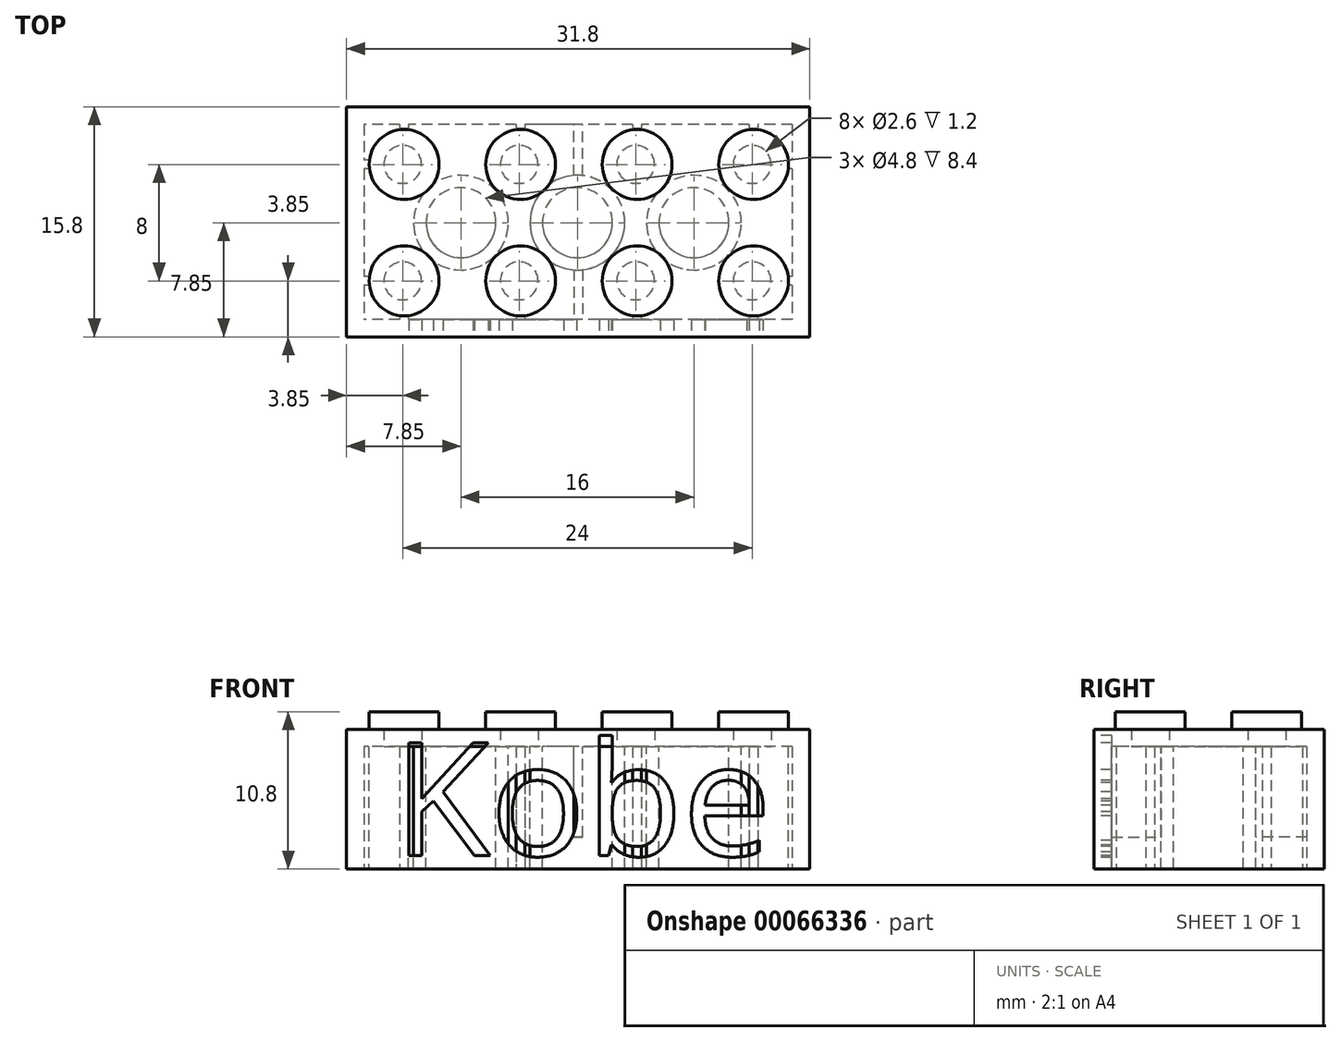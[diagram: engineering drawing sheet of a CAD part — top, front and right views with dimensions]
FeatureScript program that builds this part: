
annotation { "Feature Type Name" : "Feature", "Feature Type Description" : "" }
export const myFeature = defineFeature(function(context is Context, id is Id, definition is map)
    precondition{}
    {
        {
            var Q0;
            Q0=qCreatedBy(makeId("Top.planeOp"),FACE);
            var sketch = newSketch(context, id + "F0", { "sketchPlane" : qUnion([Q0])});
            skLineSegment(sketch, "E0.rect.bottom", {"start": v(15.9, -7.9) * mm, "end": v(-15.9, -7.9) * mm});
            skLineSegment(sketch, "E0.rect.top", {"start": v(15.9, 7.9) * mm, "end": v(-15.9, 7.9) * mm});
            skLineSegment(sketch, "E0.rect.left", {"start": v(15.9, -7.9) * mm, "end": v(15.9, 7.9) * mm});
            skLineSegment(sketch, "E0.rect.right", {"start": v(-15.9, -7.9) * mm, "end": v(-15.9, 7.9) * mm});
            skPoint(sketch, "E0.rect.middle", {"position": v(0, 0) * mm});
            skSolve(sketch);
        }
        {
            var Q0;
            Q0 = qSketchRegion(id + "F0", true);
            extrude(context, id + "F1", {"entities" : qUnion([Q0]), "depth" : 9.6 * mm});
        }
        {
            var Q0;
            Q0=makeQuery(id+"F1.opExtrude","CAP_FACE",FACE,{"disambiguationData":[OSD([sQuery(id+"F0.wireOp",EDGE,"E0.rect.bottom"),sQuery(id+"F0.wireOp",EDGE,"E0.rect.top"),sQuery(id+"F0.wireOp",EDGE,"E0.rect.left"),sQuery(id+"F0.wireOp",EDGE,"E0.rect.right")])],"isStart":true});
            var sketch = newSketch(context, id + "F2", { "sketchPlane" : qUnion([Q0])});
            skLineSegment(sketch, "E1.rect.bottom", {"start": v(14.7, -6.7) * mm, "end": v(-14.7, -6.7) * mm});
            skLineSegment(sketch, "E1.rect.top", {"start": v(14.7, 6.7) * mm, "end": v(-14.7, 6.7) * mm});
            skLineSegment(sketch, "E1.rect.left", {"start": v(14.7, -6.7) * mm, "end": v(14.7, 6.7) * mm});
            skLineSegment(sketch, "E1.rect.right", {"start": v(-14.7, -6.7) * mm, "end": v(-14.7, 6.7) * mm});
            skPoint(sketch, "E1.rect.middle", {"position": v(0, 0) * mm});
            skSolve(sketch);
        }
        {
            var Q0;
            Q0 = qSketchRegion(id + "F2", true);
            extrude(context, id + "F3", {"entities" : qUnion([Q0]), "operationType" : NewBodyOperationType.REMOVE, "oppositeDirection" : true, "depth" : 8.4 * mm});
        }
        {
            var Q0;
            Q0=makeQuery(id+"F1.opExtrude","CAP_FACE",FACE,{"disambiguationData":[OSD([sQuery(id+"F0.wireOp",EDGE,"E0.rect.bottom"),sQuery(id+"F0.wireOp",EDGE,"E0.rect.top"),sQuery(id+"F0.wireOp",EDGE,"E0.rect.left"),sQuery(id+"F0.wireOp",EDGE,"E0.rect.right")])],"isStart":false});
            var sketch = newSketch(context, id + "F4", { "sketchPlane" : qUnion([Q0])});
            skLineSegment(sketch, "E2", {"start": v(0, 0) * mm, "end": v(-19.28, 0) * mm, "construction": true});
            skLineSegment(sketch, "E3", {"start": v(-19.28, 0) * mm, "end": v(19.46, 0) * mm, "construction": true});
            skSolve(sketch);
        }
        {
            var Q0;
            Q0=makeQuery(id+"F4.imprint","IMPRINT",FACE,{"disambiguationData":[TD([[makeQuery(id+"F4.imprint","IMPRINT",EDGE,{"derivedFrom":makeQuery(id+"F1.opExtrude","CAP_EDGE",EDGE,{"disambiguationData":[OSD([sQuery(id+"F0.wireOp",EDGE,"E0.rect.bottom")])],"isStart":false})}),-1.0]])]});
            var sketch = newSketch(context, id + "F5", { "sketchPlane" : qUnion([Q0])});
            skCircle(sketch, "E4", {"center": v(-11.95, 3.95) * mm, "radius": 2.4 * mm});
            skCircle(sketch, "E5.0.1.0", {"center": v(-11.95, -4.05) * mm, "radius": 2.4 * mm});
            skCircle(sketch, "E5.1.0.0", {"center": v(-3.95, 3.95) * mm, "radius": 2.4 * mm});
            skCircle(sketch, "E5.1.1.0", {"center": v(-3.95, -4.05) * mm, "radius": 2.4 * mm});
            skCircle(sketch, "E5.2.0.0", {"center": v(4.05, 3.95) * mm, "radius": 2.4 * mm});
            skCircle(sketch, "E5.2.1.0", {"center": v(4.05, -4.05) * mm, "radius": 2.4 * mm});
            skCircle(sketch, "E5.3.0.0", {"center": v(12.05, 3.95) * mm, "radius": 2.4 * mm});
            skCircle(sketch, "E5.3.1.0", {"center": v(12.05, -4.05) * mm, "radius": 2.4 * mm});
            skLineSegment(sketch, "E5.direction1", {"start": v(-11.95, 3.95) * mm, "end": v(-3.95, 3.95) * mm, "construction": true});
            skLineSegment(sketch, "E5.direction2", {"start": v(-11.95, 3.95) * mm, "end": v(-11.95, -4.05) * mm, "construction": true});
            skSolve(sketch);
        }
        {
            var Q0;
            Q0 = qSketchRegion(id + "F5", true);
            extrude(context, id + "F6", {"entities" : qUnion([Q0]), "operationType" : NewBodyOperationType.ADD, "depth" : 1.2 * mm});
        }
        {
            var Q0;
            Q0=makeQuery(id+"F3.boolean.opBoolean","COPY",FACE,{"derivedFrom":makeQuery(id+"F3.opExtrude","CAP_FACE",FACE,{"disambiguationData":[OSD([sQuery(id+"F2.wireOp",EDGE,"E1.rect.bottom"),sQuery(id+"F2.wireOp",EDGE,"E1.rect.top"),sQuery(id+"F2.wireOp",EDGE,"E1.rect.left"),sQuery(id+"F2.wireOp",EDGE,"E1.rect.right")])],"isStart":false})});
            var sketch = newSketch(context, id + "F7", { "sketchPlane" : qUnion([Q0])});
            skCircle(sketch, "E6", {"center": v(-12.05, 4.05) * mm, "radius": 1.3 * mm});
            skCircle(sketch, "E7.0.1.0", {"center": v(-12.05, -3.95) * mm, "radius": 1.3 * mm});
            skCircle(sketch, "E7.1.0.0", {"center": v(-4.05, 4.05) * mm, "radius": 1.3 * mm});
            skCircle(sketch, "E7.1.1.0", {"center": v(-4.05, -3.95) * mm, "radius": 1.3 * mm});
            skCircle(sketch, "E7.2.0.0", {"center": v(3.95, 4.05) * mm, "radius": 1.3 * mm});
            skCircle(sketch, "E7.2.1.0", {"center": v(3.95, -3.95) * mm, "radius": 1.3 * mm});
            skCircle(sketch, "E7.3.0.0", {"center": v(11.95, 4.05) * mm, "radius": 1.3 * mm});
            skCircle(sketch, "E7.3.1.0", {"center": v(11.95, -3.95) * mm, "radius": 1.3 * mm});
            skLineSegment(sketch, "E7.direction1", {"start": v(-12.05, 4.05) * mm, "end": v(-4.05, 4.05) * mm, "construction": true});
            skLineSegment(sketch, "E7.direction2", {"start": v(-12.05, 4.05) * mm, "end": v(-12.05, -3.95) * mm, "construction": true});
            skSolve(sketch);
        }
        {
            var Q0;
            Q0 = qSketchRegion(id + "F7", true);
            extrude(context, id + "F8", {"entities" : qUnion([Q0]), "operationType" : NewBodyOperationType.REMOVE, "oppositeDirection" : true, "depth" : 1.2 * mm});
        }
        {
            var Q0;
            Q0=makeQuery(id+"F3.boolean.opBoolean","COPY",FACE,{"derivedFrom":makeQuery(id+"F3.opExtrude","CAP_FACE",FACE,{"disambiguationData":[OSD([sQuery(id+"F2.wireOp",EDGE,"E1.rect.bottom"),sQuery(id+"F2.wireOp",EDGE,"E1.rect.top"),sQuery(id+"F2.wireOp",EDGE,"E1.rect.left"),sQuery(id+"F2.wireOp",EDGE,"E1.rect.right")])],"isStart":false})});
            var sketch = newSketch(context, id + "F9", { "sketchPlane" : qUnion([Q0])});
            skLineSegment(sketch, "E8", {"start": v(-12.05, 4.05) * mm, "end": v(-4.05, -3.95) * mm, "construction": true});
            skLineSegment(sketch, "E9", {"start": v(-12.05, -3.95) * mm, "end": v(-4.05, 4.05) * mm, "construction": true});
            skLineSegment(sketch, "E10", {"start": v(3.95, 4.05) * mm, "end": v(11.95, -3.95) * mm, "construction": true});
            skLineSegment(sketch, "E11", {"start": v(3.95, -3.95) * mm, "end": v(11.95, 4.05) * mm, "construction": true});
            skLineSegment(sketch, "E12", {"start": v(-4.05, -3.95) * mm, "end": v(3.95, 4.05) * mm, "construction": true});
            skLineSegment(sketch, "E13", {"start": v(-4.05, 4.05) * mm, "end": v(3.95, -3.95) * mm, "construction": true});
            skCircle(sketch, "E14", {"center": v(-8.05, 0.05) * mm, "radius": 2.4 * mm});
            skCircle(sketch, "E15", {"center": v(-8.05, 0.05) * mm, "radius": 3.25 * mm});
            skCircle(sketch, "E16", {"center": v(-0.05, 0.05) * mm, "radius": 2.4 * mm});
            skCircle(sketch, "E17", {"center": v(-0.05, 0.05) * mm, "radius": 3.25 * mm});
            skCircle(sketch, "E18", {"center": v(7.95, 0.05) * mm, "radius": 2.4 * mm});
            skCircle(sketch, "E19", {"center": v(7.95, 0.05) * mm, "radius": 3.25 * mm});
            skSolve(sketch);
        }
        {
            var Q0;
            Q0 = qSketchRegion(id + "F9", true);
            var Q1;
            Q1=makeQuery(id+"F1.opExtrude","CAP_FACE",FACE,{"disambiguationData":[OSD([sQuery(id+"F0.wireOp",EDGE,"E0.rect.bottom"),sQuery(id+"F0.wireOp",EDGE,"E0.rect.top"),sQuery(id+"F0.wireOp",EDGE,"E0.rect.left"),sQuery(id+"F0.wireOp",EDGE,"E0.rect.right")])],"isStart":true});
            extrude(context, id + "F10", {"entities" : qUnion([Q0]), "operationType" : NewBodyOperationType.ADD, "endBound" : BoundingType.UP_TO_SURFACE, "endBoundEntityFace" : qUnion([Q1]), "depth" : 25 * mm});
        }
        {
            var Q0;
            Q0=qCreatedBy(makeId("Top.planeOp"),FACE);
            var sketch = newSketch(context, id + "F11", { "sketchPlane" : qUnion([Q0])});
            skLineSegment(sketch, "E20.bottom", {"start": v(-12.25, -6.7) * mm, "end": v(-11.65, -6.7) * mm});
            skLineSegment(sketch, "E20.top", {"start": v(-12.25, -6.4) * mm, "end": v(-11.65, -6.4) * mm});
            skLineSegment(sketch, "E20.left", {"start": v(-12.25, -6.7) * mm, "end": v(-12.25, -6.4) * mm});
            skLineSegment(sketch, "E20.right", {"start": v(-11.65, -6.7) * mm, "end": v(-11.65, -6.4) * mm});
            skLineSegment(sketch, "E21", {"start": v(-11.95, 3.95) * mm, "end": v(-11.95, -25.24) * mm, "construction": true});
            skLineSegment(sketch, "E22.0.1.0", {"start": v(-12.25, 6.7) * mm, "end": v(-11.65, 6.7) * mm});
            skLineSegment(sketch, "E22.0.1.1", {"start": v(-11.65, 6.4) * mm, "end": v(-11.65, 6.7) * mm});
            skLineSegment(sketch, "E22.0.1.2", {"start": v(-12.25, 6.4) * mm, "end": v(-11.65, 6.4) * mm});
            skLineSegment(sketch, "E22.0.1.3", {"start": v(-12.25, 6.4) * mm, "end": v(-12.25, 6.7) * mm});
            skLineSegment(sketch, "E22.1.0.0", {"start": v(-4.25, -6.4) * mm, "end": v(-3.65, -6.4) * mm});
            skLineSegment(sketch, "E22.1.0.1", {"start": v(-3.65, -6.7) * mm, "end": v(-3.65, -6.4) * mm});
            skLineSegment(sketch, "E22.1.0.2", {"start": v(-4.25, -6.7) * mm, "end": v(-3.65, -6.7) * mm});
            skLineSegment(sketch, "E22.1.0.3", {"start": v(-4.25, -6.7) * mm, "end": v(-4.25, -6.4) * mm});
            skLineSegment(sketch, "E22.1.1.0", {"start": v(-4.25, 6.7) * mm, "end": v(-3.65, 6.7) * mm});
            skLineSegment(sketch, "E22.1.1.1", {"start": v(-3.65, 6.4) * mm, "end": v(-3.65, 6.7) * mm});
            skLineSegment(sketch, "E22.1.1.2", {"start": v(-4.25, 6.4) * mm, "end": v(-3.65, 6.4) * mm});
            skLineSegment(sketch, "E22.1.1.3", {"start": v(-4.25, 6.4) * mm, "end": v(-4.25, 6.7) * mm});
            skLineSegment(sketch, "E22.2.0.0", {"start": v(3.75, -6.4) * mm, "end": v(4.35, -6.4) * mm});
            skLineSegment(sketch, "E22.2.0.1", {"start": v(4.35, -6.7) * mm, "end": v(4.35, -6.4) * mm});
            skLineSegment(sketch, "E22.2.0.2", {"start": v(3.75, -6.7) * mm, "end": v(4.35, -6.7) * mm});
            skLineSegment(sketch, "E22.2.0.3", {"start": v(3.75, -6.7) * mm, "end": v(3.75, -6.4) * mm});
            skLineSegment(sketch, "E22.2.1.0", {"start": v(3.75, 6.7) * mm, "end": v(4.35, 6.7) * mm});
            skLineSegment(sketch, "E22.2.1.1", {"start": v(4.35, 6.4) * mm, "end": v(4.35, 6.7) * mm});
            skLineSegment(sketch, "E22.2.1.2", {"start": v(3.75, 6.4) * mm, "end": v(4.35, 6.4) * mm});
            skLineSegment(sketch, "E22.2.1.3", {"start": v(3.75, 6.4) * mm, "end": v(3.75, 6.7) * mm});
            skLineSegment(sketch, "E22.3.0.0", {"start": v(11.75, -6.4) * mm, "end": v(12.35, -6.4) * mm});
            skLineSegment(sketch, "E22.3.0.1", {"start": v(12.35, -6.7) * mm, "end": v(12.35, -6.4) * mm});
            skLineSegment(sketch, "E22.3.0.2", {"start": v(11.75, -6.7) * mm, "end": v(12.35, -6.7) * mm});
            skLineSegment(sketch, "E22.3.0.3", {"start": v(11.75, -6.7) * mm, "end": v(11.75, -6.4) * mm});
            skLineSegment(sketch, "E22.3.1.0", {"start": v(11.75, 6.7) * mm, "end": v(12.35, 6.7) * mm});
            skLineSegment(sketch, "E22.3.1.1", {"start": v(12.35, 6.4) * mm, "end": v(12.35, 6.7) * mm});
            skLineSegment(sketch, "E22.3.1.2", {"start": v(11.75, 6.4) * mm, "end": v(12.35, 6.4) * mm});
            skLineSegment(sketch, "E22.3.1.3", {"start": v(11.75, 6.4) * mm, "end": v(11.75, 6.7) * mm});
            skLineSegment(sketch, "E22.direction1", {"start": v(-12.25, -6.4) * mm, "end": v(-4.25, -6.4) * mm, "construction": true});
            skLineSegment(sketch, "E22.direction2", {"start": v(-12.25, -6.4) * mm, "end": v(-12.25, 6.7) * mm, "construction": true});
            skSolve(sketch);
        }
        {
            var Q0;
            Q0 = qSketchRegion(id + "F11", true);
            var Q1;
            {var subQ0=sQuery(id+"F2.wireOp",EDGE,"E1.rect.left");var subQ1=sQuery(id+"F2.wireOp",EDGE,"E1.rect.bottom");var subQ2=sQuery(id+"F2.wireOp",EDGE,"E1.rect.top");var subQ3=sQuery(id+"F2.wireOp",EDGE,"E1.rect.right");Q1=makeQuery(id+"F10.boolean.opBoolean","SPLIT",FACE,{"disambiguationData":[TD([makeQuery(id+"F3.boolean.opBoolean","COPY",FACE,{"derivedFrom":makeQuery(id+"F3.opExtrude","SWEPT_FACE",FACE,{"disambiguationData":[OSD([subQ1])]})})])],"derivedFrom":makeQuery(id+"F3.boolean.opBoolean","COPY",FACE,{"derivedFrom":makeQuery(id+"F3.opExtrude","CAP_FACE",FACE,{"disambiguationData":[OSD([subQ1,subQ2,subQ0,subQ3])],"isStart":false})})});}
            extrude(context, id + "F12", {"entities" : qUnion([Q0]), "operationType" : NewBodyOperationType.ADD, "endBound" : BoundingType.UP_TO_SURFACE, "endBoundEntityFace" : qUnion([Q1]), "depth" : 25 * mm});
        }
        {
            var Q0;
            Q0=qCreatedBy(makeId("Top.planeOp"),FACE);
            var sketch = newSketch(context, id + "F13", { "sketchPlane" : qUnion([Q0])});
            skLineSegment(sketch, "E23", {"start": v(-11.95, -4.05) * mm, "end": v(-21.76, -4.05) * mm, "construction": true});
            skLineSegment(sketch, "E24.bottom", {"start": v(-14.7, -4.35) * mm, "end": v(-14.4, -4.35) * mm});
            skLineSegment(sketch, "E24.top", {"start": v(-14.7, -3.75) * mm, "end": v(-14.4, -3.75) * mm});
            skLineSegment(sketch, "E24.left", {"start": v(-14.7, -4.35) * mm, "end": v(-14.7, -3.75) * mm});
            skLineSegment(sketch, "E24.right", {"start": v(-14.4, -4.35) * mm, "end": v(-14.4, -3.75) * mm});
            skLineSegment(sketch, "E25.0.1.0", {"start": v(-14.7, 3.65) * mm, "end": v(-14.4, 3.65) * mm});
            skLineSegment(sketch, "E25.0.1.1", {"start": v(-14.7, 3.65) * mm, "end": v(-14.7, 4.25) * mm});
            skLineSegment(sketch, "E25.0.1.2", {"start": v(-14.4, 3.65) * mm, "end": v(-14.4, 4.25) * mm});
            skLineSegment(sketch, "E25.0.1.3", {"start": v(-14.7, 4.25) * mm, "end": v(-14.4, 4.25) * mm});
            skLineSegment(sketch, "E25.1.0.0", {"start": v(14.4, -4.35) * mm, "end": v(14.7, -4.35) * mm});
            skLineSegment(sketch, "E25.1.0.1", {"start": v(14.4, -4.35) * mm, "end": v(14.4, -3.75) * mm});
            skLineSegment(sketch, "E25.1.0.2", {"start": v(14.7, -4.35) * mm, "end": v(14.7, -3.75) * mm});
            skLineSegment(sketch, "E25.1.0.3", {"start": v(14.4, -3.75) * mm, "end": v(14.7, -3.75) * mm});
            skLineSegment(sketch, "E25.1.1.0", {"start": v(14.4, 3.65) * mm, "end": v(14.7, 3.65) * mm});
            skLineSegment(sketch, "E25.1.1.1", {"start": v(14.4, 3.65) * mm, "end": v(14.4, 4.25) * mm});
            skLineSegment(sketch, "E25.1.1.2", {"start": v(14.7, 3.65) * mm, "end": v(14.7, 4.25) * mm});
            skLineSegment(sketch, "E25.1.1.3", {"start": v(14.4, 4.25) * mm, "end": v(14.7, 4.25) * mm});
            skLineSegment(sketch, "E25.direction1", {"start": v(-14.7, -4.35) * mm, "end": v(14.4, -4.35) * mm, "construction": true});
            skLineSegment(sketch, "E25.direction2", {"start": v(-14.7, -4.35) * mm, "end": v(-14.7, 3.65) * mm, "construction": true});
            skSolve(sketch);
        }
        {
            var Q0;
            Q0 = qSketchRegion(id + "F13", true);
            var Q1;
            {var subQ0=sQuery(id+"F2.wireOp",EDGE,"E1.rect.left");var subQ1=sQuery(id+"F2.wireOp",EDGE,"E1.rect.bottom");var subQ2=sQuery(id+"F2.wireOp",EDGE,"E1.rect.top");var subQ3=sQuery(id+"F2.wireOp",EDGE,"E1.rect.right");Q1=makeQuery(id+"F10.boolean.opBoolean","SPLIT",FACE,{"disambiguationData":[TD([makeQuery(id+"F3.boolean.opBoolean","COPY",FACE,{"derivedFrom":makeQuery(id+"F3.opExtrude","SWEPT_FACE",FACE,{"disambiguationData":[OSD([subQ1])]})})])],"derivedFrom":makeQuery(id+"F3.boolean.opBoolean","COPY",FACE,{"derivedFrom":makeQuery(id+"F3.opExtrude","CAP_FACE",FACE,{"disambiguationData":[OSD([subQ1,subQ2,subQ0,subQ3])],"isStart":false})})});}
            extrude(context, id + "F14", {"entities" : qUnion([Q0]), "operationType" : NewBodyOperationType.ADD, "endBound" : BoundingType.UP_TO_SURFACE, "endBoundEntityFace" : qUnion([Q1]), "depth" : 25 * mm});
        }
        {
            var Q0;
            Q0=qCreatedBy(makeId("Top.planeOp"),FACE);
            cPlane(context, id + "F15", {"entities" : qUnion([Q0]), "cplaneType" : CPlaneType.OFFSET, "offset" : 8.6 * mm, "width" : 150 * mm, "height" : 150 * mm});
        }
        {
            var Q0;
            Q0=qCreatedBy(id+"F15.planeOp",FACE);
            var sketch = newSketch(context, id + "F16", { "sketchPlane" : qUnion([Q0])});
            skLineSegment(sketch, "E26.bottom", {"start": v(-0.3, -6.9) * mm, "end": v(0.3, -6.9) * mm});
            skLineSegment(sketch, "E26.top", {"start": v(-0.3, -2.9) * mm, "end": v(0.3, -2.9) * mm});
            skLineSegment(sketch, "E26.left", {"start": v(-0.3, -6.9) * mm, "end": v(-0.3, -2.9) * mm});
            skLineSegment(sketch, "E26.right", {"start": v(0.3, -6.9) * mm, "end": v(0.3, -2.9) * mm});
            skLineSegment(sketch, "E27.bottom", {"start": v(0.3, 6.9) * mm, "end": v(-0.3, 6.9) * mm});
            skLineSegment(sketch, "E27.top", {"start": v(0.3, 2.9) * mm, "end": v(-0.3, 2.9) * mm});
            skLineSegment(sketch, "E27.left", {"start": v(0.3, 6.9) * mm, "end": v(0.3, 2.9) * mm});
            skLineSegment(sketch, "E27.right", {"start": v(-0.3, 6.9) * mm, "end": v(-0.3, 2.9) * mm});
            skSolve(sketch);
        }
        {
            var Q0;
            Q0 = qSketchRegion(id + "F16", true);
            extrude(context, id + "F17", {"entities" : qUnion([Q0]), "operationType" : NewBodyOperationType.ADD, "oppositeDirection" : true, "depth" : 6.4 * mm});
        }
        {
            var Q0;
            Q0=makeQuery(id+"F1.opExtrude","SWEPT_FACE",FACE,{"disambiguationData":[OSD([sQuery(id+"F0.wireOp",EDGE,"E0.rect.bottom")])]});
            var sketch = newSketch(context, id + "F18", { "sketchPlane" : qUnion([Q0])});
            skText(sketch, "E28", { "text": "Kobe", "fontName": "OpenSans-Regular.ttf"});
            const initialGuessF18  = {"E28": [-0.01271, 0.00091, 1, 0, 0.00782]};
            skSetInitialGuess(sketch, initialGuessF18);
            skSolve(sketch);
        }
        {
            var Q0;
            Q0 = qSketchRegion(id + "F18", true);
            extrude(context, id + "F19", {"entities" : qUnion([Q0]), "operationType" : NewBodyOperationType.REMOVE, "oppositeDirection" : true, "depth" : 1.2 * mm});
        }
    });
